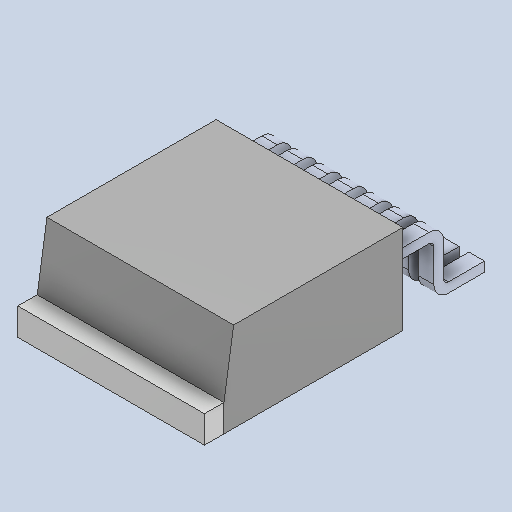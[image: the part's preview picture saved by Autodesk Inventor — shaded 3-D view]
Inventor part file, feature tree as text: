
AUTODESK INVENTOR PART (.ipt)
format: ipt  version: 2023.1 (Build 271208000, 208)  size: 171,520 bytes
history: native  units: in
note: dims shown in document units (in); Inventor stores cm internally (conversion verified against a paired STEP export)
features: other x8, fillet x1
ambient origin geometry x8: Origin, YZ Plane, XZ Plane, XY Plane, X Axis, Y Axis, Z Axis, Center Point
bodies: Solid1 (feature_tree), Solid2 (feature_tree), Solid3 (feature_tree), Solid4 (feature_tree), Solid5 (feature_tree), Solid6 (feature_tree), Solid7 (feature_tree), Solid8 (feature_tree), Solid9 (feature_tree)
feature tree (9):
  other  "Boss-Extrude1"
  other  "Boss-Extrude2"
  fillet  "Fillet2"  [1 undecoded]
  other  "LPattern3[1]"
  other  "LPattern3[2]"
  other  "LPattern3[3]"
  other  "LPattern3[4]"
  other  "LPattern3[5]"
  other  "LPattern3[6]"
note: 1 required parameter value undecoded (feature->parameter linkage not recoverable at this tier; creation-order binding heuristic only, values carry confidence <= 0.55)
